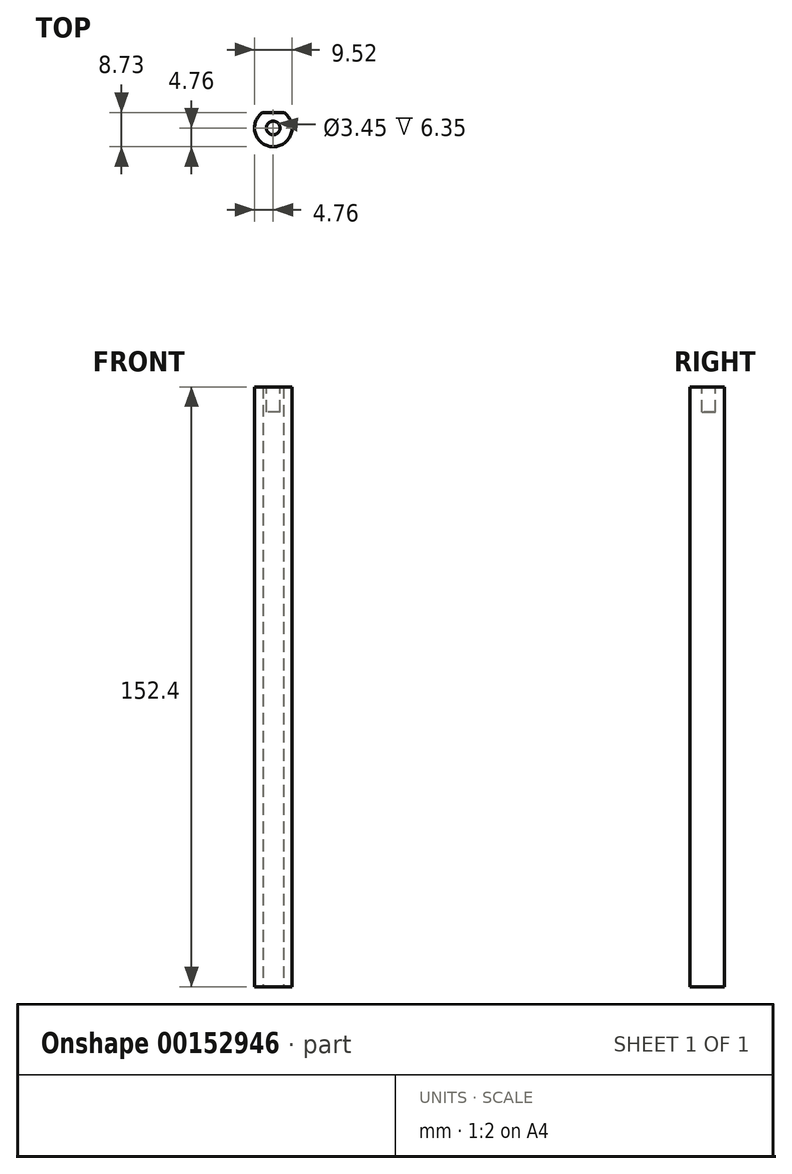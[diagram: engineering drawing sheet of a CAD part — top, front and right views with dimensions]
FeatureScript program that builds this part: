
annotation { "Feature Type Name" : "Feature", "Feature Type Description" : "" }
export const myFeature = defineFeature(function(context is Context, id is Id, definition is map)
    precondition{}
    {
        {
            var Q0;
            Q0=qCreatedBy(makeId("Top.planeOp"),FACE);
            var sketch = newSketch(context, id + "F0", { "sketchPlane" : qUnion([Q0])});
            skArc(sketch, "E0", {"start": v(-2.63, 3.97) * mm, "mid": v(0, -4.76) * mm, "end": v(2.63, 3.97) * mm});
            skLineSegment(sketch, "E1", {"start": v(0, 0) * mm, "end": v(0, 3.97) * mm, "construction": true});
            skLineSegment(sketch, "E2", {"start": v(-2.63, 3.97) * mm, "end": v(2.63, 3.97) * mm});
            skSolve(sketch);
        }
        {
            var Q0;
            Q0 = qSketchRegion(id + "F0", true);
            extrude(context, id + "F1", {"entities" : qUnion([Q0]), "depth" : 152.4 * mm});
        }
        {
            var Q0;
            Q0=makeQuery(id+"F1.opExtrude","CAP_FACE",FACE,{"disambiguationData":[OSD([sQuery(id+"F0.wireOp",EDGE,"E0"),sQuery(id+"F0.wireOp",EDGE,"E2")])],"isStart":false});
            var sketch = newSketch(context, id + "F2", { "sketchPlane" : qUnion([Q0])});
            skCircle(sketch, "E3", {"center": v(0, 0) * mm, "radius": 1.73 * mm});
            skSolve(sketch);
        }
        {
            var Q0;
            Q0 = qSketchRegion(id + "F2", true);
            extrude(context, id + "F3", {"entities" : qUnion([Q0]), "operationType" : NewBodyOperationType.REMOVE, "oppositeDirection" : true, "depth" : 6.35 * mm});
        }
    });
